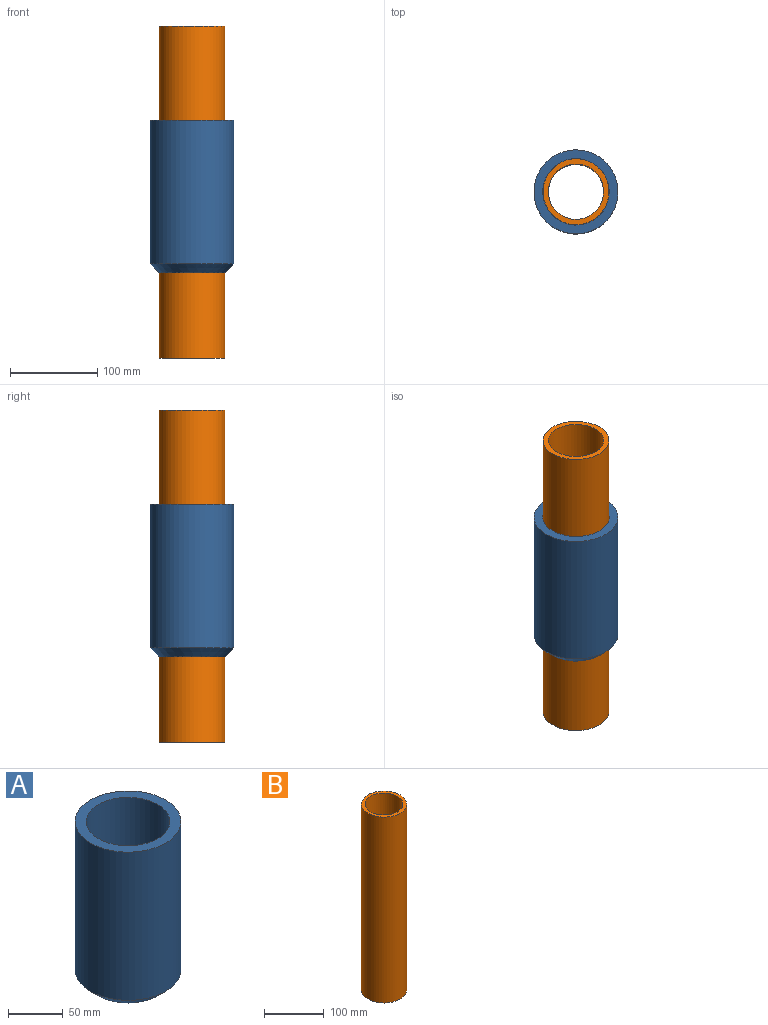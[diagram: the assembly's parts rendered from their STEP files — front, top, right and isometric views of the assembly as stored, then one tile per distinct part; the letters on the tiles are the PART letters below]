
ASSEMBLY  parts=2 mates=1
PART A: 4 faces, bbox 96.4x96.4x175.2 mm
  f0: cone r=48.21mm half-angle=45deg, axis (0,0,1), area 3878.6mm2, adj f1,f3
  f1: cylinder r=48.21mm len=165.1mm, axis (0,0,-1), area 50015.1mm2, adj f0,f2
  f2: plane 96.43x96.43mm, normal (0,0,1), area 2742.6mm2, adj f1,f3
  f3: cylinder r=38.1mm len=175.21mm, axis (0,0,1), area 41944.4mm2, adj f0,f2
PART B: 4 faces, bbox 75.7x75.7x381 mm
  f0: cylinder r=37.85mm len=381mm, axis (0,0,-1), area 90599.3mm2, adj f1,f2
  f1: plane 75.69x75.69mm, normal (0,0,1), area 1332.8mm2, adj f0,f3
  f2: plane 75.69x75.69mm, normal (0,0,-1), area 1332.8mm2, adj f0,f3
  f3: cylinder r=31.75mm len=381mm, axis (0,0,1), area 76006.1mm2, adj f1,f2
PLACE A t=(4.6,18.42,-76.52)mm
PLACE B t=(12.08,11.22,-171.77)mm
MATE slider A.f0 <-> B.f0  axis (0,0,-1) through (-19.15,42.74,18.73)mm
